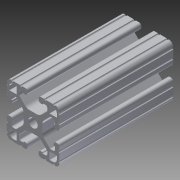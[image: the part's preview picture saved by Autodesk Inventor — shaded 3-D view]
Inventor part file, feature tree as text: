
AUTODESK INVENTOR PART (.ipt)
format: ipt  version: 2013 (Build 170138000, 138)  size: 303,104 bytes
history: native  units: in
note: dims shown in document units (in); Inventor stores cm internally (conversion verified against a paired STEP export)
features: extrude x1, sketch x1
ambient origin geometry x8: Origin, YZ Plane, XZ Plane, XY Plane, X Axis, Y Axis, Z Axis, Center Point
bodies: Solid1 (feature_tree)
feature tree (2):
  extrude  "Extrusion1"  [1 undecoded]
  sketch  "Sketch1"  dims[d0=3.25in d1=0.0in]
note: 1 required parameter value undecoded (feature->parameter linkage not recoverable at this tier; creation-order binding heuristic only, values carry confidence <= 0.55)
